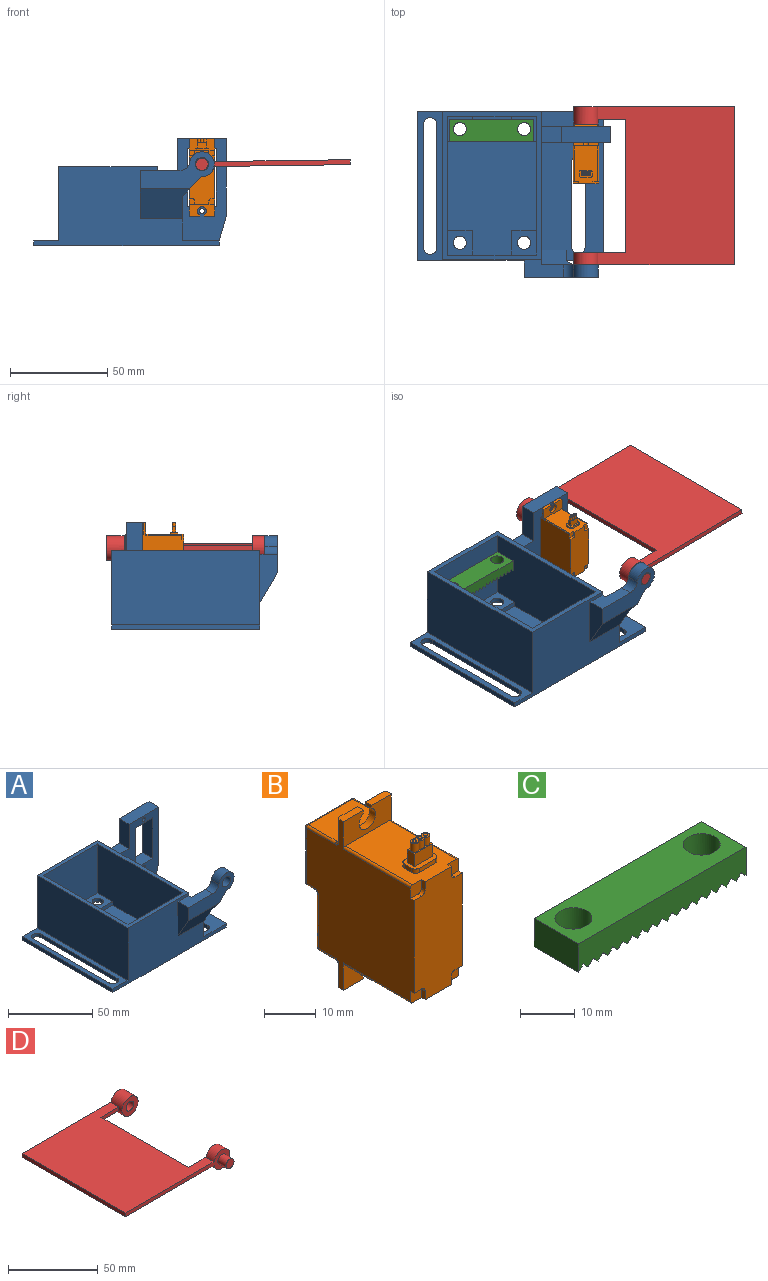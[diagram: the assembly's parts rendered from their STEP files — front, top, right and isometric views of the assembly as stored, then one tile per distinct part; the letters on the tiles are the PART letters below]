
ASSEMBLY  parts=4 mates=5
PART A: 69 faces, bbox 98.9x85.1x55.1 mm
  f0: plane 95.25x76.2mm, normal (0,0,-1), area 5885.5mm2, adj f28,f29,f30,f39,f41,f42,f43,f44
  f1: plane 71.12x45.72mm, normal (0,0,1), area 2606.4mm2, adj f2,f32,f33,f34,f49,f50,f52,f53
  f2: plane 71.12x38.1mm, normal (-1,0,0), area 2645.2mm2, adj f1,f32,f34,f36,f52,f54,f56,f57
  f3: plane 31.75x7.66mm, normal (0,0,1), area 243mm2, adj f8,f17,f30,f39
  f4: plane 10.16x10.16mm, normal (0.71,0,-0.71), area 90.4mm2, adj f5,f6,f22,f25,f37,f38
  f5: plane 38.1x19.05mm, normal (0,-1,0), area 365.4mm2, adj f4,f23,f24,f25,f26,f27,f37
  f6: plane 22.86x11.77mm, normal (1,0,0), area 121.7mm2, adj f4,f7,f21,f29,f37,f38
  f7: plane 12.7x11.27mm, normal (0,1,0), area 143.2mm2, adj f6,f8,f21,f38
  f8: plane 78.74x38.1mm, normal (1,0,0), area 2563mm2, adj f3,f7,f13,f17,f18,f21,f22,f26
  f9: plane 14.83x8.26mm, normal (0,0,1), area 122.4mm2, adj f10,f16,f17,f18
  f10: plane 29.51x8.26mm, normal (-1,0,0), area 243.6mm2, adj f9,f11,f17,f18
  f11: plane 14.83x8.26mm, normal (0,0,-1), area 122.4mm2, adj f10,f16,f17,f18
  f12: plane 40x8.26mm, normal (1,0,0), area 330.2mm2, adj f15,f17,f18,f40
  f13: plane 10.41x8.26mm, normal (0,0,1), area 85.9mm2, adj f8,f14,f17,f18
  f14: plane 17.73x8.26mm, normal (-1,0,0), area 146.3mm2, adj f13,f15,f17,f18
  f15: plane 24.99x8.26mm, normal (0,0,1), area 206.3mm2, adj f12,f14,f17,f18
  f16: plane 29.51x8.26mm, normal (1,0,0), area 243.6mm2, adj f9,f11,f17,f18
  f17: plane 52.57x35.4mm, normal (0,1,0), area 1205.8mm2, adj f3,f8,f9,f10,f11,f12,f13,f14
  f18: plane 52.57x35.4mm, normal (0,-1,0), area 1205.8mm2, adj f8,f9,f10,f11,f12,f13,f14,f15
  f19: cylinder r=1.27mm len=8.26mm, axis (0,-1,0), area 65.9mm2, adj f17,f18
  f20: cylinder r=1.27mm len=8.26mm, axis (0,-1,0), area 65.9mm2, adj f17,f18
  f21: plane 60.29x31.75mm, normal (0,0,1), area 1513.5mm2, adj f6,f7,f8,f18,f29,f39,f45,f46
  f22: plane 29.21x19.05mm, normal (0,1,0), area 280.7mm2, adj f4,f8,f23,f25,f26,f27,f38
  f23: cylinder r=3.43mm len=6.86mm, axis (0,-1,0), area 136.8mm2, adj f5,f22
  f24: plane 24.92x8.89mm, normal (-1,0,0), area 153.1mm2, adj f5,f26,f29,f37
  f25: cylinder r=6.35mm len=12.7mm, axis (0,-1,0), area 183.3mm2, adj f4,f5,f22,f27
  f26: plane 20.48x8.89mm, normal (0,0,1), area 152.6mm2, adj f5,f8,f22,f24,f27,f29
  f27: cylinder r=5.08mm len=6.35mm, axis (0,-1,0), area 45.3mm2, adj f5,f22,f25,f26
  f28: plane 76.2x2.54mm, normal (-1,0,0), area 193.5mm2, adj f0,f29,f30,f31
  f29: plane 95.25x40.64mm, normal (0,-1,0), area 2099mm2, adj f0,f6,f8,f21,f24,f26,f28,f31
  f30: plane 95.25x40.64mm, normal (0,1,0), area 2177.4mm2, adj f0,f3,f8,f28,f31,f35,f36,f39
  f31: plane 76.2x12.7mm, normal (0,0,1), area 502.9mm2, adj f28,f29,f30,f35,f41,f42,f43,f44
  f32: plane 45.72x38.1mm, normal (0,1,0), area 1677.4mm2, adj f1,f2,f33,f36,f55,f57,f59,f60
  f33: plane 71.12x38.1mm, normal (1,0,0), area 2645.2mm2, adj f1,f32,f34,f36,f49,f51,f58,f60
  f34: plane 45.72x38.1mm, normal (0,-1,0), area 1677.4mm2, adj f1,f2,f33,f36,f50,f51,f53,f54
  f35: plane 76.2x38.1mm, normal (-1,0,0), area 2903.2mm2, adj f29,f30,f31,f36
  f36: plane 76.2x50.8mm, normal (0,0,1), area 619.4mm2, adj f2,f8,f29,f30,f32,f33,f34,f35
  f37: plane 25.4x15.4mm, normal (0,-0.87,-0.5), area 392.3mm2, adj f4,f5,f6,f24,f29
  f38: plane 16.51x15.4mm, normal (0,0.9,0.44), area 226.3mm2, adj f4,f6,f7,f8,f22
  f39: plane 76.2x2.54mm, normal (1,0,0), area 193.5mm2, adj f0,f3,f21,f29,f30,f40
  f40: plane 12.57x8.26mm, normal (0.96,0,-0.28), area 108.1mm2, adj f12,f17,f18,f39
  f41: cylinder r=3.38mm len=6.76mm, axis (0,0,1), area 27mm2, adj f0,f31,f42,f44
  f42: plane 63.5x2.54mm, normal (1,0,0), area 161.3mm2, adj f0,f31,f41,f43
  f43: cylinder r=3.38mm len=6.76mm, axis (0,0,1), area 27mm2, adj f0,f31,f42,f44
  f44: plane 63.5x2.54mm, normal (-1,0,0), area 161.3mm2, adj f0,f31,f41,f43
  f45: plane 44.45x2.54mm, normal (1,0,0), area 112.9mm2, adj f0,f21,f46,f48
  f46: cylinder r=3.38mm len=6.76mm, axis (0,0,1), area 27mm2, adj f0,f21,f45,f47
  f47: plane 44.45x2.54mm, normal (-1,0,0), area 112.9mm2, adj f0,f21,f46,f48
  f48: cylinder r=3.38mm len=6.76mm, axis (0,0,1), area 27mm2, adj f0,f21,f45,f47
  f49: plane 12.7x2.54mm, normal (0,-1,0), area 32.3mm2, adj f1,f33,f50,f51
  f50: plane 12.7x2.54mm, normal (1,0,0), area 32.3mm2, adj f1,f34,f49,f51
  f51: plane 12.7x12.7mm, normal (0,0,1), area 125.4mm2, adj f33,f34,f49,f50,f67
  f52: plane 12.7x2.54mm, normal (0,-1,0), area 32.3mm2, adj f1,f2,f53,f54
  f53: plane 12.7x2.54mm, normal (-1,0,0), area 32.3mm2, adj f1,f34,f52,f54
  f54: plane 12.7x12.7mm, normal (0,0,1), area 125.4mm2, adj f2,f34,f52,f53,f65
  f55: plane 12.7x2.54mm, normal (-1,0,0), area 32.3mm2, adj f1,f32,f56,f57
  f56: plane 12.7x2.54mm, normal (0,1,0), area 32.3mm2, adj f1,f2,f55,f57
  f57: plane 12.7x12.7mm, normal (0,0,1), area 125.4mm2, adj f2,f32,f55,f56,f63
  f58: plane 12.7x2.54mm, normal (0,1,0), area 32.3mm2, adj f1,f33,f59,f60
  f59: plane 12.7x2.54mm, normal (1,0,0), area 32.3mm2, adj f1,f32,f58,f60
  f60: plane 12.7x12.7mm, normal (0,0,1), area 125.4mm2, adj f32,f33,f58,f59,f61
  f61: cylinder r=3.38mm len=6.76mm, axis (0,0,-1), area 47.9mm2, adj f60,f62
  f62: cone r=3.38mm half-angle=50deg, axis (0,0,-1), area 139.7mm2, adj f0,f61
  f63: cylinder r=3.38mm len=6.76mm, axis (0,0,-1), area 47.9mm2, adj f57,f64
  f64: cone r=3.38mm half-angle=50deg, axis (0,0,-1), area 139.7mm2, adj f0,f63
  f65: cylinder r=3.38mm len=6.76mm, axis (0,0,-1), area 47.9mm2, adj f54,f66
  f66: cone r=3.38mm half-angle=50deg, axis (0,0,-1), area 139.7mm2, adj f0,f65
  f67: cylinder r=3.38mm len=6.76mm, axis (0,0,-1), area 47.9mm2, adj f51,f68
  f68: cone r=3.38mm half-angle=50deg, axis (0,0,-1), area 139.7mm2, adj f0,f67
PART B: 119 faces, bbox 13.2x33.2x40.1 mm
  f0: plane 4.65x1.65mm, normal (0,0,1), area 4.8mm2, adj f109,f110,f111,f112,f113,f115,f117
  f1: plane 5x2mm, normal (0,0,1), area 3.7mm2, adj f105,f106,f107,f108,f109,f110,f111,f112
  f2: plane 2x1mm, normal (-1,0,0), area 2mm2, adj f8,f9,f16,f104
  f3: plane 4.5x1mm, normal (0,-1,0), area 4.5mm2, adj f6,f8,f16,f104
  f4: plane 2x1mm, normal (1,0,0), area 2mm2, adj f6,f7,f16,f104
  f5: plane 4.5x1mm, normal (0,1,0), area 4.5mm2, adj f7,f9,f16,f104
  f6: cylinder r=1mm len=1mm, axis (0,0,-1), area 1.6mm2, adj f3,f4,f16,f104
  f7: cylinder r=1mm len=1mm, axis (0,0,-1), area 1.6mm2, adj f4,f5,f16,f104
  f8: cylinder r=1mm len=1mm, axis (0,0,-1), area 1.6mm2, adj f2,f3,f16,f104
  f9: cylinder r=1mm len=1mm, axis (0,0,-1), area 1.6mm2, adj f2,f5,f16,f104
  f10: plane 17x12.2mm, normal (0,1,0), area 137mm2, adj f70,f71,f72,f74,f76,f77,f102,f103
  f11: plane 12.8x12.2mm, normal (0,1,0), area 55.4mm2, adj f78,f81,f84,f85,f86,f88,f90,f92
  f12: plane 5.5x1.7mm, normal (0,0,-1), area 9.3mm2, adj f19,f40,f41,f51,f95
  f13: plane 5.5x1.7mm, normal (0,0,1), area 9.3mm2, adj f19,f37,f38,f48,f62
  f14: plane 12.2x4.7mm, normal (0,0,-1), area 57.3mm2, adj f93,f94,f98,f99
  f15: plane 19.4x12.2mm, normal (0,0,-1), area 231.7mm2, adj f20,f24,f26,f28,f29,f40,f43,f45
  f16: plane 19.4x12.2mm, normal (0,0,1), area 206.5mm2, adj f2,f3,f4,f5,f6,f7,f8,f9
  f17: plane 12.2x7.9mm, normal (0,0,1), area 96.4mm2, adj f65,f66,f69,f70
  f18: plane 40x29.5mm, normal (1,0,0), area 763.6mm2, adj f20,f21,f23,f25,f26,f37,f39,f40
  f19: plane 40x29.5mm, normal (-1,0,0), area 763.6mm2, adj f12,f13,f20,f27,f29,f31,f32,f37
  f20: plane 28x13.2mm, normal (0,-1,0), area 334.5mm2, adj f15,f16,f18,f19,f21,f22,f24,f25
  f21: plane 2x1mm, normal (0,0,1), area 2mm2, adj f18,f20,f23,f36
  f22: plane 2x1mm, normal (1,0,0), area 2mm2, adj f16,f20,f23,f36
  f23: plane 3x3mm, normal (0,-1,0), area 8.7mm2, adj f16,f18,f21,f22,f36,f46
  f24: plane 2x1mm, normal (1,0,0), area 2mm2, adj f15,f20,f26,f34
  f25: plane 2x1mm, normal (0,0,-1), area 2mm2, adj f18,f20,f26,f34
  f26: plane 3x3mm, normal (0,-1,0), area 8.7mm2, adj f15,f18,f24,f25,f34,f45
  f27: plane 2x1mm, normal (0,0,-1), area 2mm2, adj f19,f20,f29,f33
  f28: plane 2x1mm, normal (-1,0,0), area 2mm2, adj f15,f20,f29,f33
  f29: plane 3x3mm, normal (0,-1,0), area 8.7mm2, adj f15,f19,f27,f28,f33,f43
  f30: plane 2x1mm, normal (-1,0,0), area 2mm2, adj f16,f20,f32,f35
  f31: plane 2x1mm, normal (0,0,1), area 2mm2, adj f19,f20,f32,f35
  f32: plane 3x3mm, normal (0,-1,0), area 8.7mm2, adj f16,f19,f30,f31,f35,f44
  f33: cylinder r=1mm len=1mm, axis (0,1,0), area 1.6mm2, adj f20,f27,f28,f29
  f34: cylinder r=1mm len=1mm, axis (0,1,0), area 1.6mm2, adj f20,f24,f25,f26
  f35: cylinder r=1mm len=1mm, axis (0,1,0), area 1.6mm2, adj f20,f30,f31,f32
  f36: cylinder r=1mm len=1mm, axis (0,1,0), area 1.6mm2, adj f20,f21,f22,f23
  f37: plane 13.2x6.5mm, normal (0,-1,0), area 62.3mm2, adj f13,f16,f18,f19,f39,f44,f46,f47
  f38: plane 12.2x5.5mm, normal (0,1,0), area 50.1mm2, adj f13,f39,f47,f48,f49,f62,f64,f65
  f39: plane 5.5x1.7mm, normal (0,0,1), area 9.3mm2, adj f18,f37,f38,f49,f64
  f40: plane 13.2x6.5mm, normal (0,-1,0), area 62.3mm2, adj f12,f15,f18,f19,f42,f43,f45,f50
  f41: plane 12.2x5.5mm, normal (0,1,0), area 50.1mm2, adj f12,f42,f50,f51,f52,f95,f99,f101
  f42: plane 5.5x1.7mm, normal (0,0,-1), area 9.3mm2, adj f18,f40,f41,f52,f101
  f43: cylinder r=0.5mm len=18.4mm, axis (0,-1,0), area 14.5mm2, adj f15,f19,f29,f40
  f44: cylinder r=0.5mm len=18.4mm, axis (0,-1,0), area 14.5mm2, adj f16,f19,f32,f37
  f45: cylinder r=0.5mm len=18.4mm, axis (0,-1,0), area 14.5mm2, adj f15,f18,f26,f40
  f46: cylinder r=0.5mm len=18.4mm, axis (0,-1,0), area 14.5mm2, adj f16,f18,f23,f37
  f47: cylinder r=2.25mm len=4.5mm, axis (0,1,0), area 20.1mm2, adj f37,f38,f48,f49
  f48: plane 1.7x0.69mm, normal (1,0,0), area 1.2mm2, adj f13,f37,f38,f47
  f49: plane 1.7x0.69mm, normal (-1,0,0), area 1.2mm2, adj f37,f38,f39,f47
  f50: cylinder r=2.25mm len=4.5mm, axis (0,1,0), area 20.1mm2, adj f40,f41,f51,f52
  f51: plane 1.7x0.69mm, normal (1,0,0), area 1.2mm2, adj f12,f40,f41,f50
  f52: plane 1.7x0.69mm, normal (-1,0,0), area 1.2mm2, adj f40,f41,f42,f50
  f53: plane 2.3x2.2mm, normal (0,0,-1), area 5.1mm2, adj f54,f77,f83,f84
  f54: cylinder r=3.8mm len=7.6mm, axis (0,-1,0), area 26.3mm2, adj f53,f55,f74,f81
  f55: plane 2.3x2.2mm, normal (0,0,-1), area 5.1mm2, adj f54,f71,f78,f79
  f56: plane 3x3mm, normal (0,1,0), area 7.1mm2, adj f103
  f57: plane 5.6x5.6mm, normal (0,1,0), area 21.5mm2, adj f58,f59
  f58: cylinder r=2.8mm len=5.6mm, axis (0,-1,0), area 47.5mm2, adj f57,f102
  f59: cylinder r=1mm len=3.2mm, axis (0,-1,0), area 20.1mm2, adj f57,f60
  f60: plane 2x2mm, normal (0,1,0), area 3.1mm2, adj f59
  f61: plane 10x6mm, normal (0,1,0), area 60mm2, adj f85,f88,f89,f90
  f62: cylinder r=0.5mm len=5.5mm, axis (0,0,-1), area 4.3mm2, adj f13,f19,f38,f63
  f63: torus R=1mm, axis (1,0,0), area 0.8mm2, adj f19,f62,f65,f66
  f64: cylinder r=0.5mm len=5.5mm, axis (0,0,-1), area 4.3mm2, adj f18,f38,f39,f67
  f65: cylinder r=0.5mm len=12.2mm, axis (1,0,0), area 9.6mm2, adj f17,f38,f63,f67
  f66: cylinder r=0.5mm len=7.9mm, axis (0,-1,0), area 6.2mm2, adj f17,f19,f63,f68
  f67: torus R=1mm, axis (-1,0,0), area 0.8mm2, adj f18,f64,f65,f69
  f68: sphere r=0.5mm, area 0.4mm2, adj f66,f70,f72
  f69: cylinder r=0.5mm len=7.9mm, axis (0,-1,0), area 6.2mm2, adj f17,f18,f67,f73
  f70: cylinder r=0.5mm len=12.2mm, axis (-1,0,0), area 9.6mm2, adj f10,f17,f68,f73
  f71: cylinder r=0.5mm len=2.84mm, axis (1,0,0), area 2mm2, adj f10,f55,f74,f75
  f72: cylinder r=0.5mm len=13.2mm, axis (0,0,-1), area 10.4mm2, adj f10,f19,f68,f75
  f73: sphere r=0.5mm, area 0.4mm2, adj f69,f70,f76
  f74: torus R=3.3mm, axis (0,1,0), area 9.2mm2, adj f10,f54,f71,f77
  f75: sphere r=0.5mm, area 0.4mm2, adj f71,f72,f79
  f76: cylinder r=0.5mm len=13.2mm, axis (0,0,1), area 10.4mm2, adj f10,f18,f73,f80
  f77: cylinder r=0.5mm len=2.84mm, axis (1,0,0), area 2mm2, adj f10,f53,f74,f80
  f78: cylinder r=0.5mm len=2.3mm, axis (1,0,0), area 1.7mm2, adj f11,f55,f81,f82
  f79: cylinder r=0.5mm len=2.2mm, axis (0,-1,0), area 1.7mm2, adj f19,f55,f75,f82
  f80: sphere r=0.5mm, area 0.4mm2, adj f76,f77,f83
  f81: torus R=4.3mm, axis (0,-1,0), area 9.5mm2, adj f11,f54,f78,f84
  f82: torus R=1mm, axis (1,0,0), area 0.8mm2, adj f19,f78,f79,f86
  f83: cylinder r=0.5mm len=2.2mm, axis (0,-1,0), area 1.7mm2, adj f18,f53,f80,f87
  f84: cylinder r=0.5mm len=2.3mm, axis (1,0,0), area 1.7mm2, adj f11,f53,f81,f87
  f85: cylinder r=0.5mm len=11mm, axis (1,0,0), area 8.1mm2, adj f11,f61,f88,f90
  f86: cylinder r=0.5mm len=12.8mm, axis (0,0,1), area 10.1mm2, adj f11,f19,f82,f91
  f87: torus R=1mm, axis (-1,0,0), area 0.8mm2, adj f18,f83,f84,f92
  f88: cylinder r=0.5mm len=6.96mm, axis (0,0,-1), area 5mm2, adj f11,f61,f85,f89,f93
  f89: cylinder r=0.5mm len=10.91mm, axis (-1,0,0), area 7.6mm2, adj f61,f88,f90,f93
  f90: cylinder r=0.5mm len=6.96mm, axis (0,0,1), area 5mm2, adj f11,f61,f85,f89,f93
  f91: sphere r=0.5mm, area 0.4mm2, adj f86,f93,f94
  f92: cylinder r=0.5mm len=12.8mm, axis (0,0,-1), area 10.1mm2, adj f11,f18,f87,f96
  f93: cylinder r=0.5mm len=12.2mm, axis (-1,0,0), area 9.1mm2, adj f11,f14,f88,f89,f90,f91,f96
  f94: cylinder r=0.5mm len=4.7mm, axis (0,-1,0), area 3.7mm2, adj f14,f19,f91,f97
  f95: cylinder r=0.5mm len=5.5mm, axis (0,0,1), area 4.3mm2, adj f12,f19,f41,f97
  f96: sphere r=0.5mm, area 0.4mm2, adj f92,f93,f98
  f97: torus R=1mm, axis (1,0,0), area 0.8mm2, adj f19,f94,f95,f99
  f98: cylinder r=0.5mm len=4.7mm, axis (0,-1,0), area 3.7mm2, adj f14,f18,f96,f100
  f99: cylinder r=0.5mm len=12.2mm, axis (-1,0,0), area 9.6mm2, adj f14,f41,f97,f100
  f100: torus R=1mm, axis (-1,0,0), area 0.8mm2, adj f18,f98,f99,f101
  f101: cylinder r=0.5mm len=5.5mm, axis (0,0,1), area 4.3mm2, adj f18,f41,f42,f100
  f102: torus R=3.3mm, axis (0,1,0), area 14.7mm2, adj f10,f58
  f103: torus R=1.8mm, axis (0,1,0), area 3.3mm2, adj f10,f56
  f104: plane 6.5x4mm, normal (0,0,1), area 15.1mm2, adj f2,f3,f4,f5,f6,f7,f8,f9
  f105: plane 3x2mm, normal (-1,0,0), area 6mm2, adj f1,f104,f106,f108
  f106: plane 5x3mm, normal (0,1,0), area 15mm2, adj f1,f104,f105,f107
  f107: plane 3x2mm, normal (1,0,0), area 6mm2, adj f1,f104,f106,f108
  f108: plane 5x3mm, normal (0,-1,0), area 15mm2, adj f1,f104,f105,f107
  f109: cylinder r=0.82mm len=2mm, axis (0,0,-1), area 8.9mm2, adj f0,f1,f110,f112
  f110: cylinder r=0.82mm len=2mm, axis (0,0,-1), area 3.8mm2, adj f0,f1,f109,f111
  f111: cylinder r=0.82mm len=2mm, axis (0,0,-1), area 8.9mm2, adj f0,f1,f110,f112
  f112: cylinder r=0.82mm len=2mm, axis (0,0,-1), area 3.8mm2, adj f0,f1,f109,f111
  f113: cylinder r=0.4mm len=0.8mm, axis (0,0,-1), area 0.3mm2, adj f0,f114
  f114: plane 0.8x0.8mm, normal (0,0,1), area 0.5mm2, adj f113
  f115: cylinder r=0.4mm len=0.8mm, axis (0,0,-1), area 0.3mm2, adj f0,f116
  f116: plane 0.8x0.8mm, normal (0,0,1), area 0.5mm2, adj f115
  f117: cylinder r=0.4mm len=0.8mm, axis (0,0,-1), area 0.3mm2, adj f0,f118
  f118: plane 0.8x0.8mm, normal (0,0,1), area 0.5mm2, adj f117
PART C: 49 faces, bbox 43.2x11.4x6.4 mm
  f0: cylinder r=3.38mm len=6.76mm, axis (0,0,-1), area 122.3mm2, adj f6,f7,f8,f9,f10,f23,f24,f25
  f1: cylinder r=3.38mm len=6.76mm, axis (0,0,-1), area 122.3mm2, adj f6,f11,f12,f13,f14,f15,f16,f17
  f2: plane 43.18x6.35mm, normal (0,1,0), area 246.8mm2, adj f3,f5,f6,f8,f10,f11,f12,f15
  f3: plane 11.43x6.35mm, normal (-1,0,0), area 72.6mm2, adj f2,f4,f6,f21
  f4: plane 43.18x6.35mm, normal (0,-1,0), area 246.8mm2, adj f3,f5,f6,f7,f9,f11,f13,f14
  f5: plane 11.43x6.35mm, normal (1,0,0), area 72.6mm2, adj f2,f4,f6,f22
  f6: plane 43.18x11.43mm, normal (0,0,1), area 421.8mm2, adj f0,f1,f2,f3,f4,f5
  f7: plane 4.12x1.27mm, normal (-0.71,0,-0.71), area 6.5mm2, adj f0,f4,f23,f25
  f8: plane 1.95x1.27mm, normal (0.71,0,-0.71), area 3.2mm2, adj f0,f2,f24,f26
  f9: plane 3.22x1.27mm, normal (-0.71,0,-0.71), area 5.5mm2, adj f0,f4,f25,f27
  f10: plane 2.85x1.27mm, normal (0.71,0,-0.71), area 4.2mm2, adj f0,f2,f26,f28
  f11: plane 11.43x1.27mm, normal (0.71,0,-0.71), area 16.9mm2, adj f1,f2,f4,f12,f13,f48
  f12: plane 2.85x1.27mm, normal (-0.71,0,-0.71), area 4.2mm2, adj f1,f2,f11,f15
  f13: plane 4.12x1.27mm, normal (-0.71,0,-0.71), area 6.5mm2, adj f1,f4,f11,f14
  f14: plane 3.22x1.27mm, normal (0.71,0,-0.71), area 5.5mm2, adj f1,f4,f13,f17
  f15: plane 1.95x1.27mm, normal (0.71,0,-0.71), area 3.2mm2, adj f1,f2,f12,f16
  f16: plane 1.95x1.27mm, normal (-0.71,0,-0.71), area 3.2mm2, adj f1,f2,f15,f19
  f17: plane 3.22x1.27mm, normal (-0.71,0,-0.71), area 5.5mm2, adj f1,f4,f14,f18
  f18: plane 4.12x1.27mm, normal (0.71,0,-0.71), area 6.5mm2, adj f1,f4,f17,f20
  f19: plane 2.85x1.27mm, normal (0.71,0,-0.71), area 4.2mm2, adj f1,f2,f16,f20
  f20: plane 11.43x1.27mm, normal (-0.71,0,-0.71), area 16.9mm2, adj f1,f2,f4,f18,f19,f21
  f21: plane 11.43x1.27mm, normal (0.71,0,-0.71), area 20.5mm2, adj f2,f3,f4,f20
  f22: plane 11.43x1.27mm, normal (-0.71,0,-0.71), area 20.5mm2, adj f2,f4,f5,f23
  f23: plane 11.43x1.27mm, normal (0.71,0,-0.71), area 16.9mm2, adj f0,f2,f4,f7,f22,f24
  f24: plane 2.85x1.27mm, normal (-0.71,0,-0.71), area 4.2mm2, adj f0,f2,f8,f23
  f25: plane 3.22x1.27mm, normal (0.71,0,-0.71), area 5.5mm2, adj f0,f4,f7,f9
  f26: plane 1.95x1.27mm, normal (-0.71,0,-0.71), area 3.2mm2, adj f0,f2,f8,f10
  f27: plane 4.12x1.27mm, normal (0.71,0,-0.71), area 6.5mm2, adj f0,f4,f9,f28
  f28: plane 11.43x1.27mm, normal (-0.71,0,-0.71), area 16.9mm2, adj f0,f2,f4,f10,f27,f29
  f29: plane 11.43x1.27mm, normal (0.71,0,-0.71), area 20.5mm2, adj f2,f4,f28,f30
  f30: plane 11.43x1.27mm, normal (-0.71,0,-0.71), area 20.5mm2, adj f2,f4,f29,f31
  f31: plane 11.43x1.27mm, normal (0.71,0,-0.71), area 20.5mm2, adj f2,f4,f30,f32
  f32: plane 11.43x1.27mm, normal (-0.71,0,-0.71), area 20.5mm2, adj f2,f4,f31,f33
  f33: plane 11.43x1.27mm, normal (0.71,0,-0.71), area 20.5mm2, adj f2,f4,f32,f34
  f34: plane 11.43x1.27mm, normal (-0.71,0,-0.71), area 20.5mm2, adj f2,f4,f33,f35
  f35: plane 11.43x1.27mm, normal (0.71,0,-0.71), area 20.5mm2, adj f2,f4,f34,f36
  f36: plane 11.43x1.27mm, normal (-0.71,0,-0.71), area 20.5mm2, adj f2,f4,f35,f37
  f37: plane 11.43x1.27mm, normal (0.71,0,-0.71), area 20.5mm2, adj f2,f4,f36,f38
  f38: plane 11.43x1.27mm, normal (-0.71,0,-0.71), area 20.5mm2, adj f2,f4,f37,f39
  f39: plane 11.43x1.27mm, normal (0.71,0,-0.71), area 20.5mm2, adj f2,f4,f38,f40
  f40: plane 11.43x1.27mm, normal (-0.71,0,-0.71), area 20.5mm2, adj f2,f4,f39,f41
  f41: plane 11.43x1.27mm, normal (0.71,0,-0.71), area 20.5mm2, adj f2,f4,f40,f42
  f42: plane 11.43x1.27mm, normal (-0.71,0,-0.71), area 20.5mm2, adj f2,f4,f41,f43
  f43: plane 11.43x1.27mm, normal (0.71,0,-0.71), area 20.5mm2, adj f2,f4,f42,f44
  f44: plane 11.43x1.27mm, normal (-0.71,0,-0.71), area 20.5mm2, adj f2,f4,f43,f45
  f45: plane 11.43x1.27mm, normal (0.71,0,-0.71), area 20.5mm2, adj f2,f4,f44,f46
  f46: plane 11.43x1.27mm, normal (-0.71,0,-0.71), area 20.5mm2, adj f2,f4,f45,f47
  f47: plane 11.43x1.27mm, normal (0.71,0,-0.71), area 20.5mm2, adj f2,f4,f46,f48
  f48: plane 11.43x1.27mm, normal (-0.71,0,-0.71), area 20.5mm2, adj f2,f4,f11,f47
PART D: 14 faces, bbox 82.6x87.6x12.7 mm
  f0: plane 68.58x2.54mm, normal (1,0,0), area 174.2mm2, adj f4,f5,f7,f9
  f1: plane 81.28x2.54mm, normal (-1,0,0), area 206.5mm2, adj f2,f3,f4,f5
  f2: plane 82.55x12.7mm, normal (0,-1,0), area 272.5mm2, adj f1,f4,f5,f8,f10
  f3: plane 82.55x12.7mm, normal (0,1,0), area 275mm2, adj f1,f4,f5,f6,f12
  f4: plane 81.28x69.98mm, normal (0,0,1), area 4721mm2, adj f0,f1,f2,f3,f6,f7,f8,f9
  f5: plane 81.28x69.98mm, normal (0,0,-1), area 4721mm2, adj f0,f1,f2,f3,f6,f7,f8,f9
  f6: cylinder r=6.35mm len=12.7mm, axis (0,1,0), area 338.5mm2, adj f3,f4,f5,f7,f13
  f7: plane 14.1x2.54mm, normal (0,-1,0), area 35.6mm2, adj f0,f4,f5,f6
  f8: cylinder r=6.35mm len=12.7mm, axis (0,-1,0), area 237.1mm2, adj f2,f4,f5,f9
  f9: plane 26.67x12.7mm, normal (0,1,0), area 162.3mm2, adj f0,f4,f5,f8
  f10: cylinder r=3.17mm len=6.35mm, axis (0,1,0), area 126.7mm2, adj f2,f11
  f11: plane 6.35x6.35mm, normal (0,-1,0), area 31.7mm2, adj f10
  f12: cylinder r=3.05mm len=8.89mm, axis (0,-1,0), area 170.3mm2, adj f3,f13
  f13: plane 12.7x12.7mm, normal (0,-1,0), area 97.5mm2, adj f6,f12
PLACE A t=(17.58,70.17,56.84)mm fixed
PLACE B t=(17.58,70.17,56.84)mm
PLACE C t=(17.58,70.17,77.08)mm
PLACE D rot(axis=(0,1,0),179.2deg) t=(189.73,70.17,141.81)mm
MATE cylindrical C.f1 <-> A.f67  axis (0,0,1) through (39.17,137.48,88.51)mm
MATE cylindrical C.f0 <-> A.f65  axis (0,0,-1) through (72.19,137.48,88.51)mm
MATE planar D.f10 <-> A.f22  axis (0,-1,0) through (103.94,67.63,98.75)mm
MATE cylindrical A.f23 <-> D.f6  axis (0,1,0) through (103.94,67.63,98.75)mm
MATE revolute B.f47 <-> A.f20  axis (0,1,0) through (103.94,130.46,109.3)mm
